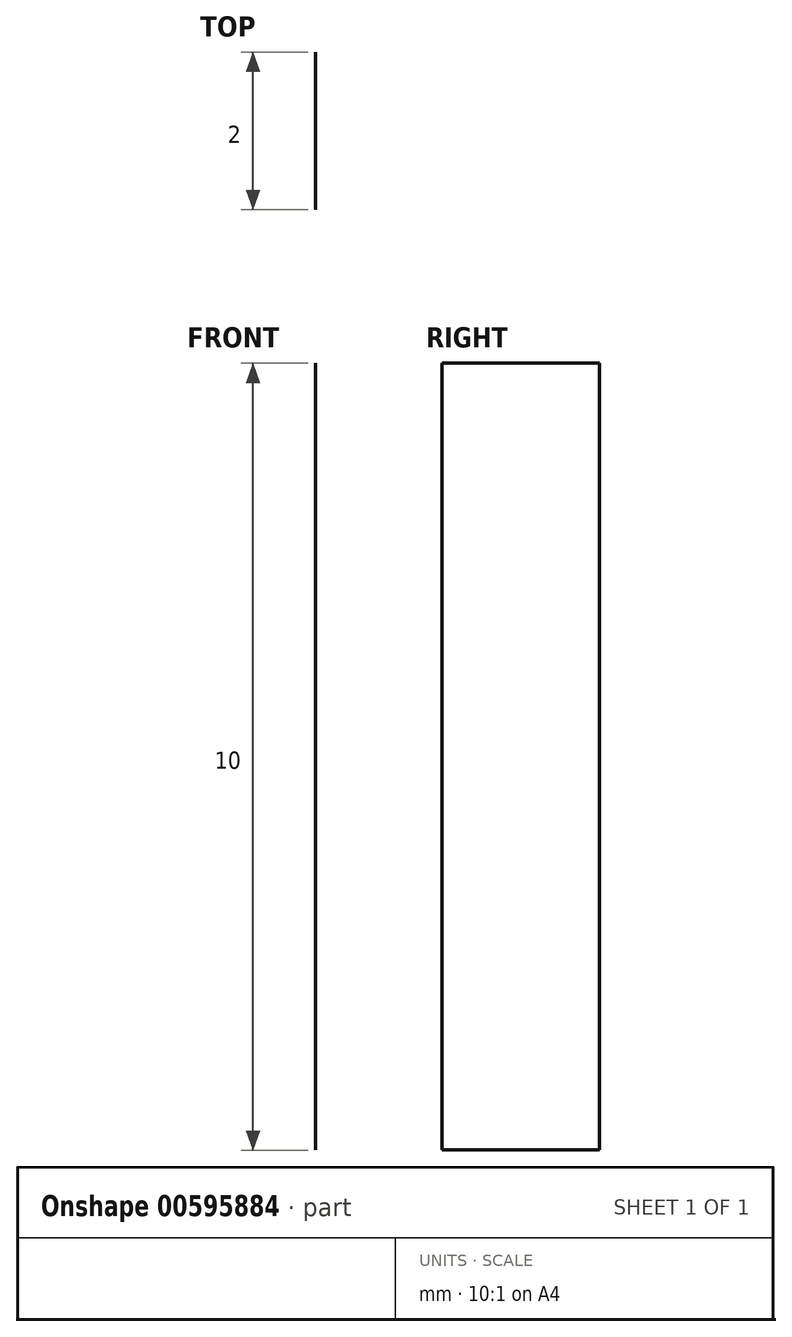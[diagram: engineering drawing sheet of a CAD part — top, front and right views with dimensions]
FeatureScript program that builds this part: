
annotation { "Feature Type Name" : "Feature", "Feature Type Description" : "" }
export const myFeature = defineFeature(function(context is Context, id is Id, definition is map)
    precondition{}
    {
        {
            var Q0;
            Q0=qCreatedBy(makeId("Front.planeOp"),FACE);
            var sketch = newSketch(context, id + "F0", { "sketchPlane" : qUnion([Q0])});
            skLineSegment(sketch, "E0", {"start": v(-55.95, 42.97) * mm, "end": v(-55.95, 32.97) * mm});
            skSolve(sketch);
        }
        {
            var Q0;
            Q0=sQuery(id+"F0.wireOp",EDGE,"E0");
            extrude(context, id + "F1", {"bodyType" : ToolBodyType.SURFACE, "surfaceEntities" : qUnion([Q0]), "depth" : 2 * mm, "offsetDistance" : 25 * mm});
        }
    });
